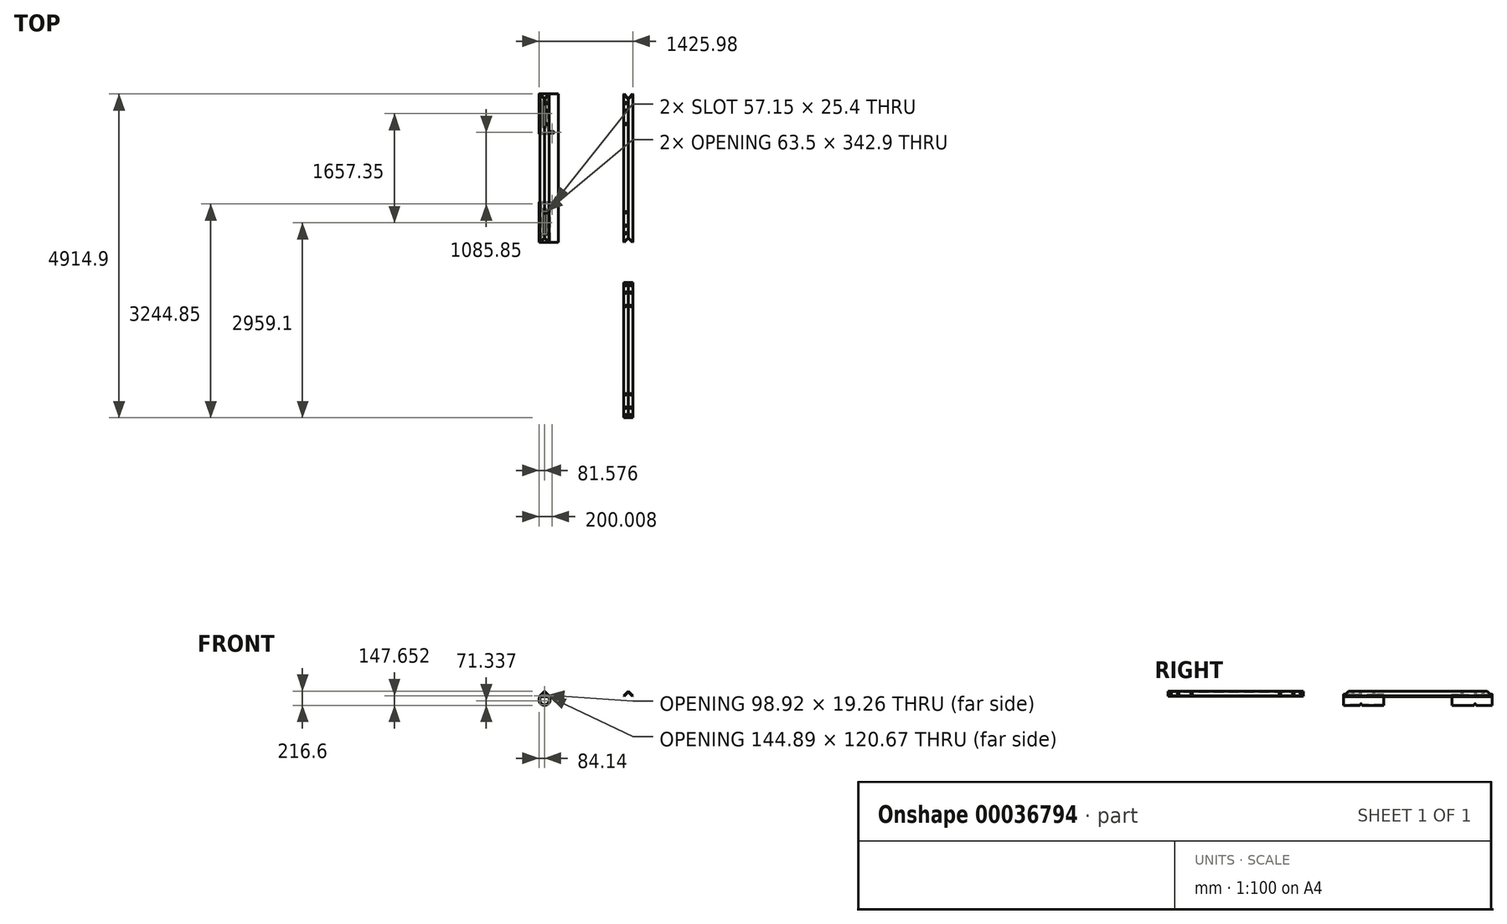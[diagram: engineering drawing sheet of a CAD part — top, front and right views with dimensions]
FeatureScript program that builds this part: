
annotation { "Feature Type Name" : "Feature", "Feature Type Description" : "" }
export const myFeature = defineFeature(function(context is Context, id is Id, definition is map)
    precondition{}
    {
        {
            var Q0;
            Q0=qCreatedBy(makeId("Front.planeOp"),FACE);
            var sketch = newSketch(context, id + "F0", { "sketchPlane" : qUnion([Q0])});
            skLineSegment(sketch, "E0", {"start": v(0, 0) * mm, "end": v(-71.84, -71.84) * mm});
            skLineSegment(sketch, "E1", {"start": v(-71.84, -71.84) * mm, "end": v(-65.1, -78.58) * mm});
            skLineSegment(sketch, "E2", {"start": v(-65.1, -78.58) * mm, "end": v(-4.5, -17.96) * mm});
            skLineSegment(sketch, "E3.MirrorCS", {"start": v(0, 0) * mm, "end": v(71.84, -71.84) * mm});
            skLineSegment(sketch, "E4.MirrorCS", {"start": v(65.1, -78.58) * mm, "end": v(4.5, -17.96) * mm});
            skLineSegment(sketch, "E5.MirrorCS", {"start": v(71.84, -71.84) * mm, "end": v(65.1, -78.58) * mm});
            skPoint(sketch, "E6.visualSharp", {"position": v(0, -13.47) * mm});
            skArc(sketch, "E6.filletArc", {"start": v(4.5, -17.96) * mm, "mid": v(0, -16.1) * mm, "end": v(-4.5, -17.96) * mm});
            skSolve(sketch);
        }
        {
            var Q0;
            Q0 = qSketchRegion(id + "F0", true);
            var Q1;
            Q1=makeQuery(id+"F0.imprint","IMPRINT",FACE,{"disambiguationData":[TD([[makeQuery(id+"F0.imprint","IMPRINT",EDGE,{"derivedFrom":sQuery(id+"F0.wireOp",EDGE,"E0")}),1.0]])]});
            extrude(context, id + "F1", {"entities" : qUnion([Q0, Q1]), "depth" : 2051.05 * mm});
        }
        {
            var Q0;
            Q0=makeQuery(id+"F1.opExtrude","SWEPT_FACE",FACE,{"disambiguationData":[OSD([sQuery(id+"F0.wireOp",EDGE,"E3.MirrorCS")])]});
            var sketch = newSketch(context, id + "F2", { "sketchPlane" : qUnion([Q0])});
            skCircle(sketch, "E7", {"center": v(-2012.95, -50.8) * mm, "radius": 12.7 * mm});
            skCircle(sketch, "E8", {"center": v(-1898.65, -50.8) * mm, "radius": 12.7 * mm});
            skCircle(sketch, "E9", {"center": v(-1695.45, -50.8) * mm, "radius": 12.7 * mm});
            skCircle(sketch, "E10", {"center": v(-38.1, -50.8) * mm, "radius": 12.7 * mm});
            skCircle(sketch, "E11", {"center": v(-152.4, -50.8) * mm, "radius": 12.7 * mm});
            skCircle(sketch, "E12", {"center": v(-355.6, -50.8) * mm, "radius": 12.7 * mm});
            skSolve(sketch);
        }
        {
            var Q0;
            Q0=makeQuery(id+"F2.imprint","IMPRINT",FACE,{"disambiguationData":[TD([[makeQuery(id+"F2.imprint","IMPRINT",EDGE,{"derivedFrom":sQuery(id+"F2.wireOp",EDGE,"E7")}),1.0]])]});
            var Q1;
            Q1=makeQuery(id+"F2.imprint","IMPRINT",FACE,{"disambiguationData":[TD([[makeQuery(id+"F2.imprint","IMPRINT",EDGE,{"derivedFrom":sQuery(id+"F2.wireOp",EDGE,"E8")}),1.0]])]});
            var Q2;
            Q2=makeQuery(id+"F2.imprint","IMPRINT",FACE,{"disambiguationData":[TD([[makeQuery(id+"F2.imprint","IMPRINT",EDGE,{"derivedFrom":sQuery(id+"F2.wireOp",EDGE,"E9")}),1.0]])]});
            var Q3;
            Q3=makeQuery(id+"F2.imprint","IMPRINT",FACE,{"disambiguationData":[TD([[makeQuery(id+"F2.imprint","IMPRINT",EDGE,{"derivedFrom":sQuery(id+"F2.wireOp",EDGE,"E12")}),1.0]])]});
            var Q4;
            Q4=makeQuery(id+"F2.imprint","IMPRINT",FACE,{"disambiguationData":[TD([[makeQuery(id+"F2.imprint","IMPRINT",EDGE,{"derivedFrom":sQuery(id+"F2.wireOp",EDGE,"E11")}),1.0]])]});
            var Q5;
            Q5=makeQuery(id+"F2.imprint","IMPRINT",FACE,{"disambiguationData":[TD([[makeQuery(id+"F2.imprint","IMPRINT",EDGE,{"derivedFrom":sQuery(id+"F2.wireOp",EDGE,"E10")}),1.0]])]});
            extrude(context, id + "F3", {"entities" : qUnion([Q0, Q1, Q2, Q3, Q4, Q5]), "operationType" : NewBodyOperationType.REMOVE, "endBound" : BoundingType.UP_TO_NEXT, "oppositeDirection" : true, "depth" : 25.4 * mm});
        }
        {
            var Q0;
            Q0=makeQuery(id+"F1.opExtrude","SWEPT_FACE",FACE,{"disambiguationData":[OSD([sQuery(id+"F0.wireOp",EDGE,"E0")])]});
            var sketch = newSketch(context, id + "F4", { "sketchPlane" : qUnion([Q0])});
            skCircle(sketch, "E13", {"center": v(2012.95, -50.8) * mm, "radius": 12.7 * mm});
            skCircle(sketch, "E14", {"center": v(1898.65, -50.8) * mm, "radius": 12.7 * mm});
            skCircle(sketch, "E15", {"center": v(1695.45, -50.8) * mm, "radius": 12.7 * mm});
            skCircle(sketch, "E16", {"center": v(38.1, -50.8) * mm, "radius": 12.7 * mm});
            skCircle(sketch, "E17", {"center": v(152.4, -50.8) * mm, "radius": 12.7 * mm});
            skCircle(sketch, "E18", {"center": v(355.6, -50.8) * mm, "radius": 12.7 * mm});
            skSolve(sketch);
        }
        {
            var Q0;
            Q0 = qSketchRegion(id + "F4", true);
            extrude(context, id + "F5", {"entities" : qUnion([Q0]), "operationType" : NewBodyOperationType.REMOVE, "endBound" : BoundingType.UP_TO_NEXT, "oppositeDirection" : true, "depth" : 25.4 * mm});
        }
        {
            var Q0;
            Q0=qCreatedBy(makeId("Front.planeOp"),FACE);
            cPlane(context, id + "F6", {"entities" : qUnion([Q0]), "cplaneType" : CPlaneType.OFFSET, "offset" : 609.6 * mm, "oppositeDirection" : true, "width" : 152.4 * mm, "height" : 152.4 * mm});
        }
        {
            var Q0;
            Q0=qCreatedBy(id+"F6.planeOp",FACE);
            var sketch = newSketch(context, id + "F7", { "sketchPlane" : qUnion([Q0])});
            skLineSegment(sketch, "E19.0", {"start": v(0, 0) * mm, "end": v(71.84, -71.84) * mm});
            skLineSegment(sketch, "E20.0", {"start": v(71.84, -71.84) * mm, "end": v(65.1, -78.58) * mm});
            skLineSegment(sketch, "E21.0", {"start": v(65.1, -78.58) * mm, "end": v(4.5, -17.96) * mm});
            skArc(sketch, "E22.0", {"start": v(4.5, -17.96) * mm, "mid": v(0, -16.1) * mm, "end": v(-4.5, -17.96) * mm});
            skLineSegment(sketch, "E23.0", {"start": v(-65.1, -78.58) * mm, "end": v(-4.5, -17.96) * mm});
            skLineSegment(sketch, "E24.0", {"start": v(-71.84, -71.84) * mm, "end": v(-65.1, -78.58) * mm});
            skLineSegment(sketch, "E25.0", {"start": v(0, 0) * mm, "end": v(-71.84, -71.84) * mm});
            skSolve(sketch);
        }
        {
            var Q0;
            Q0 = qSketchRegion(id + "F7", true);
            extrude(context, id + "F8", {"entities" : qUnion([Q0]), "oppositeDirection" : true, "depth" : 2254.25 * mm});
        }
        {
            var Q0;
            Q0=qCreatedBy(makeId("Right.planeOp"),FACE);
            var sketch = newSketch(context, id + "F9", { "sketchPlane" : qUnion([Q0])});
            skLineSegment(sketch, "E26", {"start": v(699.64, 18.2) * mm, "end": v(539.5, 54.4) * mm});
            skLineSegment(sketch, "E27", {"start": v(539.5, 54.4) * mm, "end": v(505.06, -98.01) * mm});
            skLineSegment(sketch, "E28", {"start": v(2713.25, 72.03) * mm, "end": v(2914.54, 60.38) * mm});
            skLineSegment(sketch, "E29", {"start": v(2914.54, 60.38) * mm, "end": v(2932.59, -102.83) * mm});
            skPoint(sketch, "E30.0", {"position": v(2863.85, -78.58) * mm});
            skLineSegment(sketch, "E31", {"start": v(2863.85, -78.58) * mm, "end": v(2713.25, 72.03) * mm});
            skLineSegment(sketch, "E32.0", {"start": v(2863.85, -78.58) * mm, "end": v(609.6, -78.58) * mm});
            skLineSegment(sketch, "E33", {"start": v(2863.85, -78.58) * mm, "end": v(2932.59, -102.83) * mm});
            skLineSegment(sketch, "E34", {"start": v(699.64, 18.2) * mm, "end": v(609.6, -78.58) * mm});
            skLineSegment(sketch, "E35", {"start": v(505.06, -98.01) * mm, "end": v(609.6, -78.58) * mm});
            skSolve(sketch);
        }
        {
            var Q0;
            Q0 = qSketchRegion(id + "F9", true);
            extrude(context, id + "F10", {"entities" : qUnion([Q0]), "operationType" : NewBodyOperationType.REMOVE, "endBound" : BoundingType.THROUGH_ALL, "oppositeDirection" : true, "depth" : 25.4 * mm, "hasSecondDirection" : true, "secondDirectionBound" : SecondDirectionBoundingType.THROUGH_ALL, "secondDirectionOppositeDirection" : false, "secondDirectionDepth" : 25.4 * mm});
        }
        {
            var Q0;
            Q0=makeQuery(id+"F8.opExtrude","SWEPT_FACE",FACE,{"disambiguationData":[OSD([sQuery(id+"F7.wireOp",EDGE,"E25.0")])]});
            var sketch = newSketch(context, id + "F11", { "sketchPlane" : qUnion([Q0])});
            skCircle(sketch, "E36", {"center": v(-2724.15, -50.8) * mm, "radius": 12.7 * mm});
            skCircle(sketch, "E37", {"center": v(-2609.85, -50.8) * mm, "radius": 12.7 * mm});
            skCircle(sketch, "E38", {"center": v(-2406.65, -50.8) * mm, "radius": 12.7 * mm});
            skCircle(sketch, "E39", {"center": v(-749.3, -50.8) * mm, "radius": 12.7 * mm});
            skCircle(sketch, "E40", {"center": v(-863.6, -50.8) * mm, "radius": 12.7 * mm});
            skCircle(sketch, "E41", {"center": v(-1066.8, -50.8) * mm, "radius": 12.7 * mm});
            skPoint(sketch, "E42.0", {"position": v(-2863.85, -101.6) * mm});
            skPoint(sketch, "E43.0", {"position": v(-609.6, -101.6) * mm});
            skSolve(sketch);
        }
        {
            var Q0;
            Q0 = qSketchRegion(id + "F11", true);
            extrude(context, id + "F12", {"entities" : qUnion([Q0]), "operationType" : NewBodyOperationType.REMOVE, "endBound" : BoundingType.UP_TO_NEXT, "oppositeDirection" : true, "depth" : 25.4 * mm});
        }
        {
            var Q0;
            Q0=makeQuery(id+"F8.opExtrude","CAP_VERTEX",VERTEX,{"disambiguationData":[OSD([sQuery(id+"F7.wireOp",EDGE,"E23.0"),sQuery(id+"F7.wireOp",EDGE,"E24.0")])],"isStart":false});
            var Q1;
            Q1=makeQuery(id+"F8.opExtrude","SWEPT_EDGE",EDGE,{"disambiguationData":[OSD([sQuery(id+"F7.wireOp",EDGE,"E24.0"),sQuery(id+"F7.wireOp",EDGE,"E25.0")])]});
            cPlane(context, id + "F13", {"entities" : qUnion([Q0, Q1]), "cplaneType" : CPlaneType.LINE_POINT, "offset" : 152.4 * mm, "width" : 152.4 * mm, "height" : 152.4 * mm});
        }
        {
            var Q0;
            Q0=qCreatedBy(id+"F13.planeOp",FACE);
            var sketch = newSketch(context, id + "F14", { "sketchPlane" : qUnion([Q0])});
            skPoint(sketch, "E44.0", {"position": v(65.1, -78.58) * mm});
            skPoint(sketch, "E45.0", {"position": v(-65.1, -78.58) * mm});
            skLineSegment(sketch, "E46", {"start": v(65.1, -78.58) * mm, "end": v(65.1, -84.93) * mm});
            skLineSegment(sketch, "E47", {"start": v(65.1, -84.93) * mm, "end": v(-207.65, -84.93) * mm});
            skLineSegment(sketch, "E48", {"start": v(-207.65, -84.93) * mm, "end": v(-207.65, -78.58) * mm});
            skLineSegment(sketch, "E49", {"start": v(-207.65, -78.58) * mm, "end": v(65.1, -78.58) * mm});
            skSolve(sketch);
        }
        {
            var Q0;
            Q0 = qSketchRegion(id + "F14", true);
            extrude(context, id + "F15", {"entities" : qUnion([Q0]), "depth" : 2254.25 * mm});
        }
        {
            var Q0;
            Q0=qCreatedBy(makeId("Right.planeOp"),FACE);
            cPlane(context, id + "F16", {"entities" : qUnion([Q0]), "cplaneType" : CPlaneType.OFFSET, "offset" : 635 * mm, "oppositeDirection" : true, "width" : 152.4 * mm, "height" : 152.4 * mm});
        }
        {
            var Q0;
            Q0=makeQuery(id+"F15.opExtrude","SWEPT_FACE",FACE,{"disambiguationData":[OSD([sQuery(id+"F14.wireOp",EDGE,"E49")])]});
            var sketch = newSketch(context, id + "F17", { "sketchPlane" : qUnion([Q0])});
            skLineSegment(sketch, "E50", {"start": v(-19.66, 2393.95) * mm, "end": v(24.79, 2393.95) * mm});
            skLineSegment(sketch, "E51", {"start": v(34.31, 2403.48) * mm, "end": v(34.31, 2727.33) * mm});
            skLineSegment(sketch, "E52", {"start": v(-19.66, 2736.85) * mm, "end": v(24.79, 2736.85) * mm});
            skLineSegment(sketch, "E53", {"start": v(-29.19, 2403.48) * mm, "end": v(-29.19, 2727.33) * mm});
            skPoint(sketch, "E54.visualSharp", {"position": v(34.31, 2393.95) * mm});
            skArc(sketch, "E54.filletArc", {"start": v(24.79, 2393.95) * mm, "mid": v(31.52, 2396.74) * mm, "end": v(34.31, 2403.48) * mm});
            skPoint(sketch, "E55.visualSharp", {"position": v(34.31, 2736.85) * mm});
            skArc(sketch, "E55.filletArc", {"start": v(34.31, 2727.33) * mm, "mid": v(31.52, 2734.06) * mm, "end": v(24.79, 2736.85) * mm});
            skPoint(sketch, "E56.visualSharp", {"position": v(-29.19, 2393.95) * mm});
            skArc(sketch, "E56.filletArc", {"start": v(-29.19, 2403.48) * mm, "mid": v(-26.4, 2396.74) * mm, "end": v(-19.66, 2393.95) * mm});
            skPoint(sketch, "E57.visualSharp", {"position": v(-29.19, 2736.85) * mm});
            skArc(sketch, "E57.filletArc", {"start": v(-19.66, 2736.85) * mm, "mid": v(-26.4, 2734.06) * mm, "end": v(-29.19, 2727.33) * mm});
            skLineSegment(sketch, "E58", {"start": v(-29.19, 746.13) * mm, "end": v(-29.19, 1069.98) * mm});
            skLineSegment(sketch, "E59", {"start": v(-19.66, 1079.5) * mm, "end": v(24.79, 1079.5) * mm});
            skLineSegment(sketch, "E60", {"start": v(34.31, 1069.98) * mm, "end": v(34.31, 746.13) * mm});
            skLineSegment(sketch, "E61", {"start": v(24.79, 736.6) * mm, "end": v(-19.66, 736.6) * mm});
            skPoint(sketch, "E62.visualSharp", {"position": v(34.31, 736.6) * mm});
            skArc(sketch, "E62.filletArc", {"start": v(24.79, 736.6) * mm, "mid": v(31.52, 739.39) * mm, "end": v(34.31, 746.13) * mm});
            skPoint(sketch, "E63.visualSharp", {"position": v(-29.19, 736.6) * mm});
            skArc(sketch, "E63.filletArc", {"start": v(-29.19, 746.13) * mm, "mid": v(-26.4, 739.39) * mm, "end": v(-19.66, 736.6) * mm});
            skPoint(sketch, "E64.visualSharp", {"position": v(-29.19, 1079.5) * mm});
            skArc(sketch, "E64.filletArc", {"start": v(-19.66, 1079.5) * mm, "mid": v(-26.4, 1076.71) * mm, "end": v(-29.19, 1069.98) * mm});
            skPoint(sketch, "E65.visualSharp", {"position": v(34.31, 1079.5) * mm});
            skArc(sketch, "E65.filletArc", {"start": v(34.31, 1069.98) * mm, "mid": v(31.52, 1076.71) * mm, "end": v(24.79, 1079.5) * mm});
            skArc(sketch, "E66", {"start": v(-131.74, 2292.35) * mm, "mid": v(-144.44, 2279.65) * mm, "end": v(-131.74, 2266.95) * mm});
            skLineSegment(sketch, "E67", {"start": v(-207.65, 1736.72) * mm, "end": v(-120.68, 1736.72) * mm});
            skPoint(sketch, "E67.endSnap0", {"position": v(-207.65, 1736.72) * mm});
            skArc(sketch, "E68", {"start": v(-100, 2266.95) * mm, "mid": v(-87.3, 2279.65) * mm, "end": v(-100, 2292.35) * mm});
            skLineSegment(sketch, "E69", {"start": v(-100, 2266.95) * mm, "end": v(-131.74, 2266.95) * mm});
            skLineSegment(sketch, "E70", {"start": v(-131.74, 2292.35) * mm, "end": v(-100, 2292.35) * mm});
            skArc(sketch, "E71.MirrorCS", {"start": v(-100, 1206.5) * mm, "mid": v(-87.3, 1193.8) * mm, "end": v(-100, 1181.1) * mm});
            skLineSegment(sketch, "E72.MirrorCS", {"start": v(-100, 1206.5) * mm, "end": v(-131.74, 1206.5) * mm});
            skLineSegment(sketch, "E73.MirrorCS", {"start": v(-131.74, 1181.1) * mm, "end": v(-100, 1181.1) * mm});
            skArc(sketch, "E74.MirrorCS", {"start": v(-131.74, 1181.1) * mm, "mid": v(-144.44, 1193.8) * mm, "end": v(-131.74, 1206.5) * mm});
            skSolve(sketch);
        }
        {
            var Q0;
            Q0 = qSketchRegion(id + "F17", true);
            extrude(context, id + "F18", {"entities" : qUnion([Q0]), "operationType" : NewBodyOperationType.REMOVE, "endBound" : BoundingType.UP_TO_NEXT, "oppositeDirection" : true, "depth" : 25.4 * mm});
        }
        {
            var Q0;
            Q0=qCreatedBy(id+"F13.planeOp",FACE);
            var sketch = newSketch(context, id + "F19", { "sketchPlane" : qUnion([Q0])});
            skCircle(sketch, "E75", {"center": v(0, -132.46) * mm, "radius": 84.14 * mm});
            skCircle(sketch, "E76.0", {"center": v(0, -132.46) * mm, "radius": 73.14 * mm});
            skSolve(sketch);
        }
        {
            var Q0;
            Q0=makeQuery(id+"F8.opExtrude","SWEPT_BODY",BODY,{"disambiguationData":[OSD([sQuery(id+"F7.wireOp",EDGE,"E19.0"),sQuery(id+"F7.wireOp",EDGE,"E20.0"),sQuery(id+"F7.wireOp",EDGE,"E21.0"),sQuery(id+"F7.wireOp",EDGE,"E22.0"),sQuery(id+"F7.wireOp",EDGE,"E23.0"),sQuery(id+"F7.wireOp",EDGE,"E24.0"),sQuery(id+"F7.wireOp",EDGE,"E25.0")])]});
            var Q1;
            Q1=makeQuery(id+"F15.opExtrude","SWEPT_BODY",BODY,{"disambiguationData":[OSD([sQuery(id+"F14.wireOp",EDGE,"E46"),sQuery(id+"F14.wireOp",EDGE,"E47"),sQuery(id+"F14.wireOp",EDGE,"E48"),sQuery(id+"F14.wireOp",EDGE,"E49")])]});
            var Q2;
            Q2=qCreatedBy(id+"F16.planeOp",FACE);
            mirror(context, id + "F20", {"entities" : qUnion([Q0, Q1]), "mirrorPlane" : qUnion([Q2])});
        }
        {
            var Q0;
            Q0=makeQuery(id+"F19.imprint","IMPRINT",FACE,{"disambiguationData":[TD([[makeQuery(id+"F19.imprint","IMPRINT",EDGE,{"derivedFrom":sQuery(id+"F19.wireOp",EDGE,"E75")}),1.0]])]});
            extrude(context, id + "F21", {"entities" : qUnion([Q0]), "operationType" : NewBodyOperationType.ADD, "depth" : 609.6 * mm});
        }
        {
            var Q0;
            Q0=makeQuery(id+"F8.opExtrude","CAP_VERTEX",VERTEX,{"disambiguationData":[OSD([sQuery(id+"F7.wireOp",EDGE,"E20.0"),sQuery(id+"F7.wireOp",EDGE,"E21.0")])],"isStart":false});
            var Q1;
            Q1=makeQuery(id+"F8.opExtrude","CAP_VERTEX",VERTEX,{"disambiguationData":[OSD([sQuery(id+"F7.wireOp",EDGE,"E23.0"),sQuery(id+"F7.wireOp",EDGE,"E24.0")])],"isStart":false});
            var Q2;
            Q2=makeQuery(id+"F8.opExtrude","CAP_VERTEX",VERTEX,{"disambiguationData":[OSD([sQuery(id+"F7.wireOp",EDGE,"E23.0"),sQuery(id+"F7.wireOp",EDGE,"E24.0")])],"isStart":true});
            cPlane(context, id + "F22", {"entities" : qUnion([Q0, Q1, Q2]), "cplaneType" : CPlaneType.THREE_POINT, "offset" : 152.4 * mm, "width" : 152.4 * mm, "height" : 152.4 * mm});
        }
        {
            var Q0;
            Q0=qCreatedBy(id+"F22.planeOp",FACE);
            var sketch = newSketch(context, id + "F23", { "sketchPlane" : qUnion([Q0])});
            skLineSegment(sketch, "E77.0", {"start": v(65.1, -2863.85) * mm, "end": v(4.5, -2803.23) * mm});
            skLineSegment(sketch, "E78.0", {"start": v(-65.1, -2863.85) * mm, "end": v(-4.5, -2803.23) * mm});
            skLineSegment(sketch, "E79.0.0", {"start": v(71.84, -2857.11) * mm, "end": v(0, -2785.27) * mm});
            skLineSegment(sketch, "E79.0.1", {"start": v(0, -2785.27) * mm, "end": v(0, -2355.85) * mm});
            skLineSegment(sketch, "E79.0.2", {"start": v(0, -682.7) * mm, "end": v(71.84, -615.87) * mm});
            skLineSegment(sketch, "E79.0.3", {"start": v(71.84, -615.87) * mm, "end": v(71.84, -2857.11) * mm});
            skLineSegment(sketch, "E80", {"start": v(25.4, -2762.25) * mm, "end": v(-25.4, -2762.25) * mm});
            skLineSegment(sketch, "E81", {"start": v(-31.75, -2755.9) * mm, "end": v(-31.75, -2362.2) * mm});
            skPoint(sketch, "E81.endSnap0", {"position": v(-31.75, -2406.65) * mm});
            skLineSegment(sketch, "E82", {"start": v(-25.4, -2355.85) * mm, "end": v(25.4, -2355.85) * mm});
            skLineSegment(sketch, "E83", {"start": v(31.75, -2362.2) * mm, "end": v(31.75, -2755.9) * mm});
            skPoint(sketch, "E84.visualSharp", {"position": v(31.75, -2355.85) * mm});
            skArc(sketch, "E84.filletArc", {"start": v(31.75, -2362.2) * mm, "mid": v(29.9, -2357.7) * mm, "end": v(25.4, -2355.85) * mm});
            skPoint(sketch, "E85.visualSharp", {"position": v(-31.75, -2355.85) * mm});
            skArc(sketch, "E85.filletArc", {"start": v(-25.4, -2355.85) * mm, "mid": v(-29.9, -2357.7) * mm, "end": v(-31.75, -2362.2) * mm});
            skPoint(sketch, "E86.visualSharp", {"position": v(31.75, -2762.25) * mm});
            skArc(sketch, "E86.filletArc", {"start": v(25.4, -2762.25) * mm, "mid": v(29.9, -2760.4) * mm, "end": v(31.75, -2755.9) * mm});
            skPoint(sketch, "E87.visualSharp", {"position": v(-31.75, -2762.25) * mm});
            skArc(sketch, "E87.filletArc", {"start": v(-31.75, -2755.9) * mm, "mid": v(-29.9, -2760.4) * mm, "end": v(-25.4, -2762.25) * mm});
            skSolve(sketch);
        }
        {
            var Q0;
            Q0 = qSketchRegion(id + "F23", true);
            var Q1;
            Q1=makeQuery(id+"F21.opExtrude","SWEPT_FACE",FACE,{"disambiguationData":[OSD([sQuery(id+"F19.wireOp",EDGE,"E75")])]});
            var Q2;
            Q2=makeQuery(id+"F21.opExtrude","SWEPT_BODY",BODY,{"disambiguationData":[OSD([sQuery(id+"F19.wireOp",EDGE,"E75"),sQuery(id+"F19.wireOp",EDGE,"E76.0")])]});
            extrude(context, id + "F24", {"entities" : qUnion([Q0]), "operationType" : NewBodyOperationType.REMOVE, "endBound" : BoundingType.UP_TO_SURFACE, "oppositeDirection" : true, "endBoundEntityFace" : qUnion([Q1]), "endBoundEntityBody" : qUnion([Q2]), "depth" : 25.4 * mm});
        }
        {
            var Q0;
            Q0=makeQuery(id+"F8.opExtrude","SWEPT_FACE",FACE,{"disambiguationData":[OSD([sQuery(id+"F7.wireOp",EDGE,"E25.0")])]});
            var sketch = newSketch(context, id + "F25", { "sketchPlane" : qUnion([Q0])});
            skPoint(sketch, "E88", {"position": v(-1736.73, 0) * mm});
            skSolve(sketch);
        }
        {
            var Q0;
            Q0=sQuery(id+"F25.wireOp",VERTEX,"E88");
            var Q1;
            Q1=makeQuery(id+"F8.opExtrude","SWEPT_EDGE",EDGE,{"disambiguationData":[OSD([sQuery(id+"F7.wireOp",EDGE,"E19.0"),sQuery(id+"F7.wireOp",EDGE,"E25.0")])]});
            cPlane(context, id + "F26", {"entities" : qUnion([Q0, Q1]), "cplaneType" : CPlaneType.LINE_POINT, "offset" : 152.4 * mm, "width" : 152.4 * mm, "height" : 152.4 * mm});
        }
        {
            var Q0;
            Q0=qCreatedBy(id+"F22.planeOp",FACE);
            cPlane(context, id + "F27", {"entities" : qUnion([Q0]), "cplaneType" : CPlaneType.OFFSET, "offset" : 152.4 * mm, "width" : 152.4 * mm, "height" : 152.4 * mm});
        }
        {
            var Q0;
            Q0=qCreatedBy(id+"F27.planeOp",FACE);
            var sketch = newSketch(context, id + "F28", { "sketchPlane" : qUnion([Q0])});
            skPoint(sketch, "E89.0", {"position": v(65.1, -2863.85) * mm});
            skPoint(sketch, "E90.0", {"position": v(0, -2785.27) * mm});
            skArc(sketch, "E91.1.0.0", {"start": v(38.1, -2617.6) * mm, "mid": v(53.97, -2601.72) * mm, "end": v(38.1, -2585.85) * mm});
            skLineSegment(sketch, "E91.direction1", {"start": v(0, -2601.72) * mm, "end": v(38.1, -2601.72) * mm, "construction": true});
            skLineSegment(sketch, "E92", {"start": v(38.1, -2585.85) * mm, "end": v(0, -2585.85) * mm});
            skLineSegment(sketch, "E93", {"start": v(38.1, -2617.6) * mm, "end": v(0, -2617.6) * mm});
            skLineSegment(sketch, "E94.0", {"start": v(-84.14, -2863.85) * mm, "end": v(84.14, -2863.85) * mm});
            skLineSegment(sketch, "E95.MirrorCS", {"start": v(-38.1, -2585.85) * mm, "end": v(0, -2585.85) * mm});
            skArc(sketch, "E96.MirrorCS", {"start": v(-38.1, -2617.6) * mm, "mid": v(-53.97, -2601.72) * mm, "end": v(-38.1, -2585.85) * mm});
            skLineSegment(sketch, "E97.MirrorCS", {"start": v(-38.1, -2617.6) * mm, "end": v(0, -2617.6) * mm});
            skSolve(sketch);
        }
        {
            var Q0;
            Q0 = qSketchRegion(id + "F28", true);
            var Q1;
            Q1=makeQuery(id+"F21.opExtrude","SWEPT_FACE",FACE,{"disambiguationData":[OSD([sQuery(id+"F19.wireOp",EDGE,"E76.0")])]});
            extrude(context, id + "F29", {"entities" : qUnion([Q0]), "operationType" : NewBodyOperationType.REMOVE, "endBound" : BoundingType.UP_TO_SURFACE, "oppositeDirection" : true, "endBoundEntityFace" : qUnion([Q1]), "depth" : 25.4 * mm});
        }
        {
            var Q0;
            Q0=makeQuery(id+"F21.opExtrude","SWEPT_BODY",BODY,{"disambiguationData":[OSD([sQuery(id+"F19.wireOp",EDGE,"E75"),sQuery(id+"F19.wireOp",EDGE,"E76.0")])]});
            var Q1;
            Q1=qCreatedBy(id+"F26.planeOp",FACE);
            mirror(context, id + "F30", {"operationType" : NewBodyOperationType.ADD, "entities" : qUnion([Q0]), "mirrorPlane" : qUnion([Q1])});
        }
        {
            var Q0;
            Q0=makeQuery(id+"F21.opExtrude","SWEPT_BODY",BODY,{"disambiguationData":[OSD([sQuery(id+"F19.wireOp",EDGE,"E75"),sQuery(id+"F19.wireOp",EDGE,"E76.0")])]});
            var Q1;
            Q1=makeQuery(id+"F30.opPattern","COPY",BODY,{"derivedFrom":makeQuery(id+"F21.opExtrude","SWEPT_BODY",BODY,{"disambiguationData":[OSD([sQuery(id+"F19.wireOp",EDGE,"E75"),sQuery(id+"F19.wireOp",EDGE,"E76.0")])]}),"instanceName":"1"});
            var Q2;
            Q2=qCreatedBy(id+"F16.planeOp",FACE);
            mirror(context, id + "F31", {"operationType" : NewBodyOperationType.ADD, "entities" : qUnion([Q0, Q1]), "mirrorPlane" : qUnion([Q2])});
        }
        {
            var Q0;
            Q0=makeQuery(id+"F15.opExtrude","SWEPT_BODY",BODY,{"disambiguationData":[OSD([sQuery(id+"F14.wireOp",EDGE,"E46"),sQuery(id+"F14.wireOp",EDGE,"E47"),sQuery(id+"F14.wireOp",EDGE,"E48"),sQuery(id+"F14.wireOp",EDGE,"E49")])]});
            deleteBodies(context, id + "F32", {"entities" : qUnion([Q0])});
        }
    });
